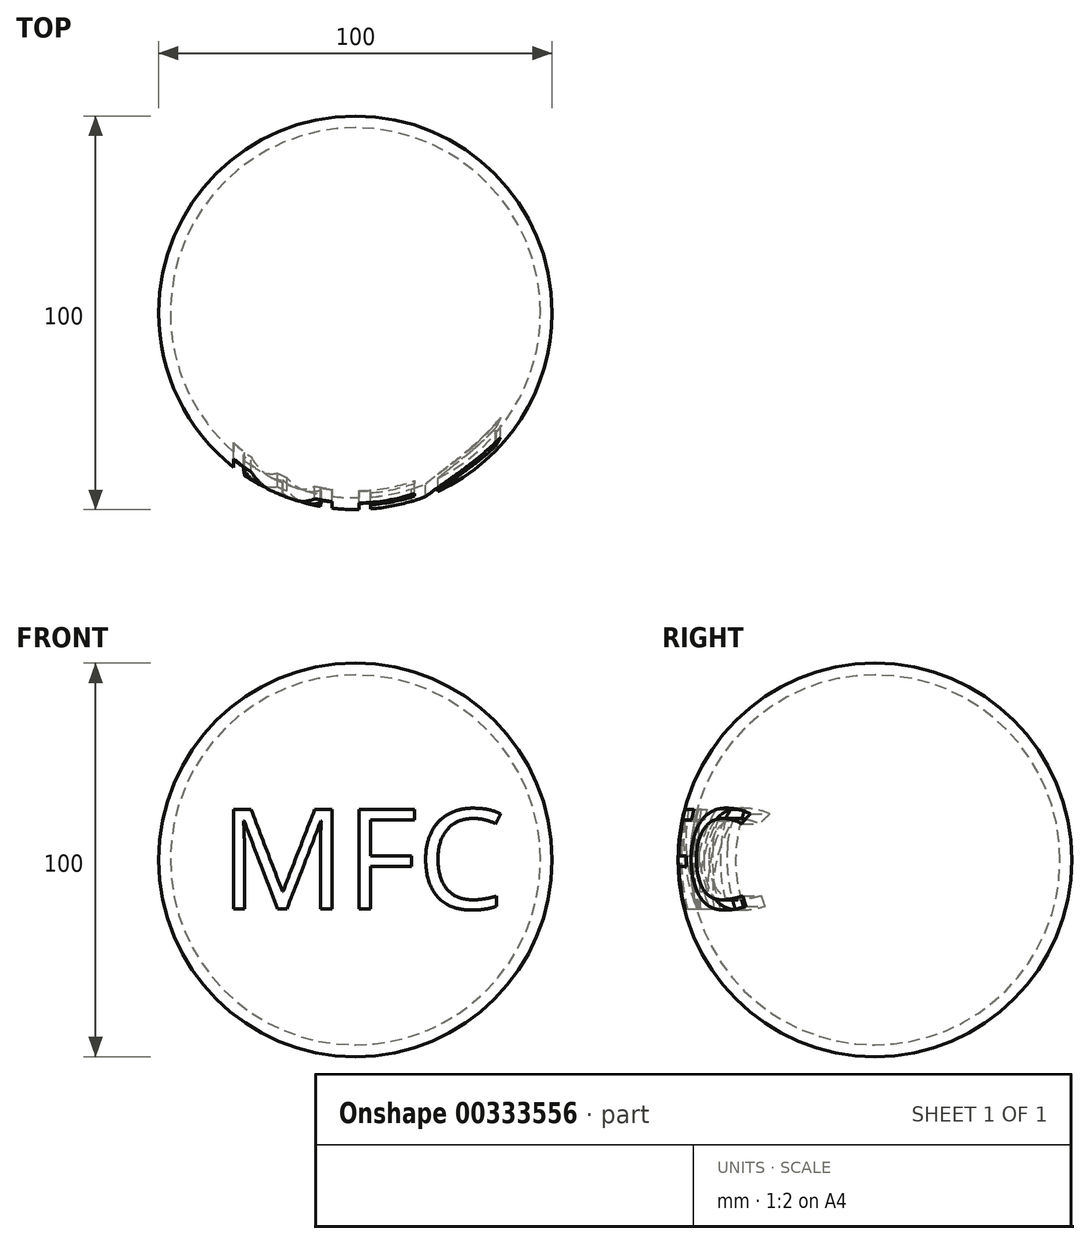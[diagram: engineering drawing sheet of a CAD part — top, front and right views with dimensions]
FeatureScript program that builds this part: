
annotation { "Feature Type Name" : "Feature", "Feature Type Description" : "" }
export const myFeature = defineFeature(function(context is Context, id is Id, definition is map)
    precondition{}
    {
        {
            var Q0;
            Q0=qCreatedBy(makeId("Front.planeOp"),FACE);
            var sketch = newSketch(context, id + "F0", { "sketchPlane" : qUnion([Q0])});
            skArc(sketch, "E0", {"start": v(50, 0) * mm, "mid": v(0, 50) * mm, "end": v(-50, 0) * mm});
            skLineSegment(sketch, "E1", {"start": v(0, 0) * mm, "end": v(50, 0) * mm});
            skLineSegment(sketch, "E2", {"start": v(0, 0) * mm, "end": v(-50, 0) * mm});
            skArc(sketch, "E3.0", {"start": v(47, 0) * mm, "mid": v(0, 47) * mm, "end": v(-47, 0) * mm});
            skSolve(sketch);
        }
        {
            var Q0;
            {var subQ0=sQuery(id+"F0.wireOp",EDGE,"E0");Q0=makeQuery(id+"F0.imprint","IMPRINT",FACE,{"disambiguationData":[TD([[makeQuery(id+"F0.imprint","IMPRINT",EDGE,{"derivedFrom":subQ0}),1.0]])]});}
            var Q1;
            Q1=sQuery(id+"F0.wireOp",EDGE,"E2");
            revolve(context, id + "F1", {"entities" : qUnion([Q0]), "axis" : qUnion([Q1]), "revolveType" : RevolveType.FULL});
        }
        {
            var Q0;
            Q0=qCreatedBy(makeId("Front.planeOp"),FACE);
            var sketch = newSketch(context, id + "F2", { "sketchPlane" : qUnion([Q0])});
            skText(sketch, "E4", { "text": "MFC", "fontName": "OpenSans-Regular.ttf"});
            const initialGuessF2  = {"E4": [-0.03437, -0.0124, 1, 0, 0.0254]};
            skSetInitialGuess(sketch, initialGuessF2);
            skSolve(sketch);
        }
        {
            var Q0;
            Q0 = qSketchRegion(id + "F2", true);
            extrude(context, id + "F3", {"entities" : qUnion([Q0]), "operationType" : NewBodyOperationType.REMOVE, "endBound" : BoundingType.THROUGH_ALL, "depth" : 25 * mm});
        }
    });
